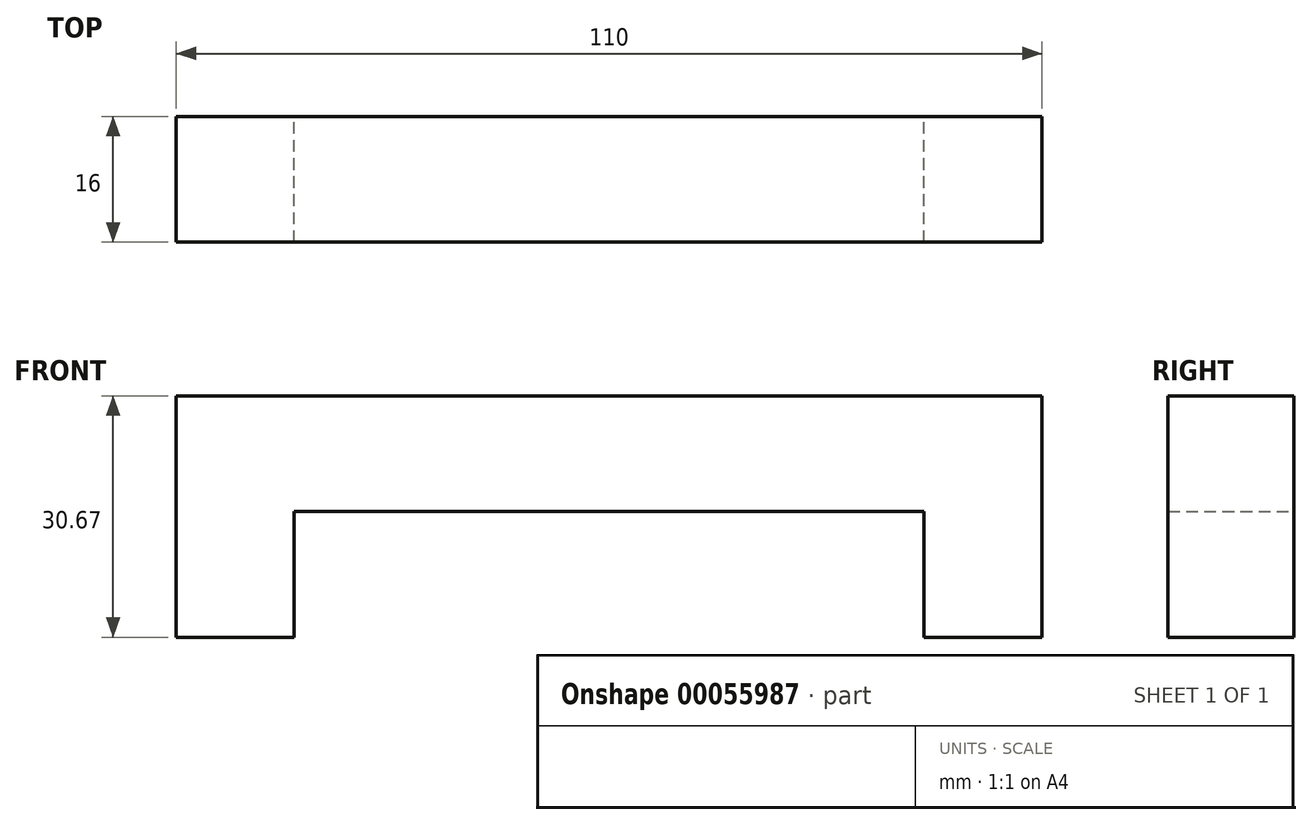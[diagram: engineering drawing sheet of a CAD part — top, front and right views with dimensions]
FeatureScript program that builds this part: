
annotation { "Feature Type Name" : "Feature", "Feature Type Description" : "" }
export const myFeature = defineFeature(function(context is Context, id is Id, definition is map)
    precondition{}
    {
        {
            var Q0;
            Q0=qCreatedBy(makeId("Front.planeOp"),FACE);
            var sketch = newSketch(context, id + "F0", { "sketchPlane" : qUnion([Q0])});
            skLineSegment(sketch, "E0", {"start": v(0, 0) * mm, "end": v(0, 30.67) * mm});
            skLineSegment(sketch, "E1", {"start": v(0, 30.67) * mm, "end": v(110, 30.67) * mm});
            skLineSegment(sketch, "E2", {"start": v(110, 30.67) * mm, "end": v(110, 0) * mm});
            skLineSegment(sketch, "E3", {"start": v(110, 0) * mm, "end": v(95, 0) * mm});
            skLineSegment(sketch, "E4", {"start": v(95, 0) * mm, "end": v(95, 16) * mm});
            skLineSegment(sketch, "E5", {"start": v(0, 0) * mm, "end": v(15, 0) * mm});
            skLineSegment(sketch, "E6", {"start": v(15, 0) * mm, "end": v(15, 16) * mm});
            skLineSegment(sketch, "E7", {"start": v(15, 16) * mm, "end": v(95, 16) * mm});
            skSolve(sketch);
        }
        {
            var Q0;
            Q0 = qSketchRegion(id + "F0", true);
            extrude(context, id + "F1", {"entities" : qUnion([Q0]), "depth" : 16 * mm});
        }
    });
